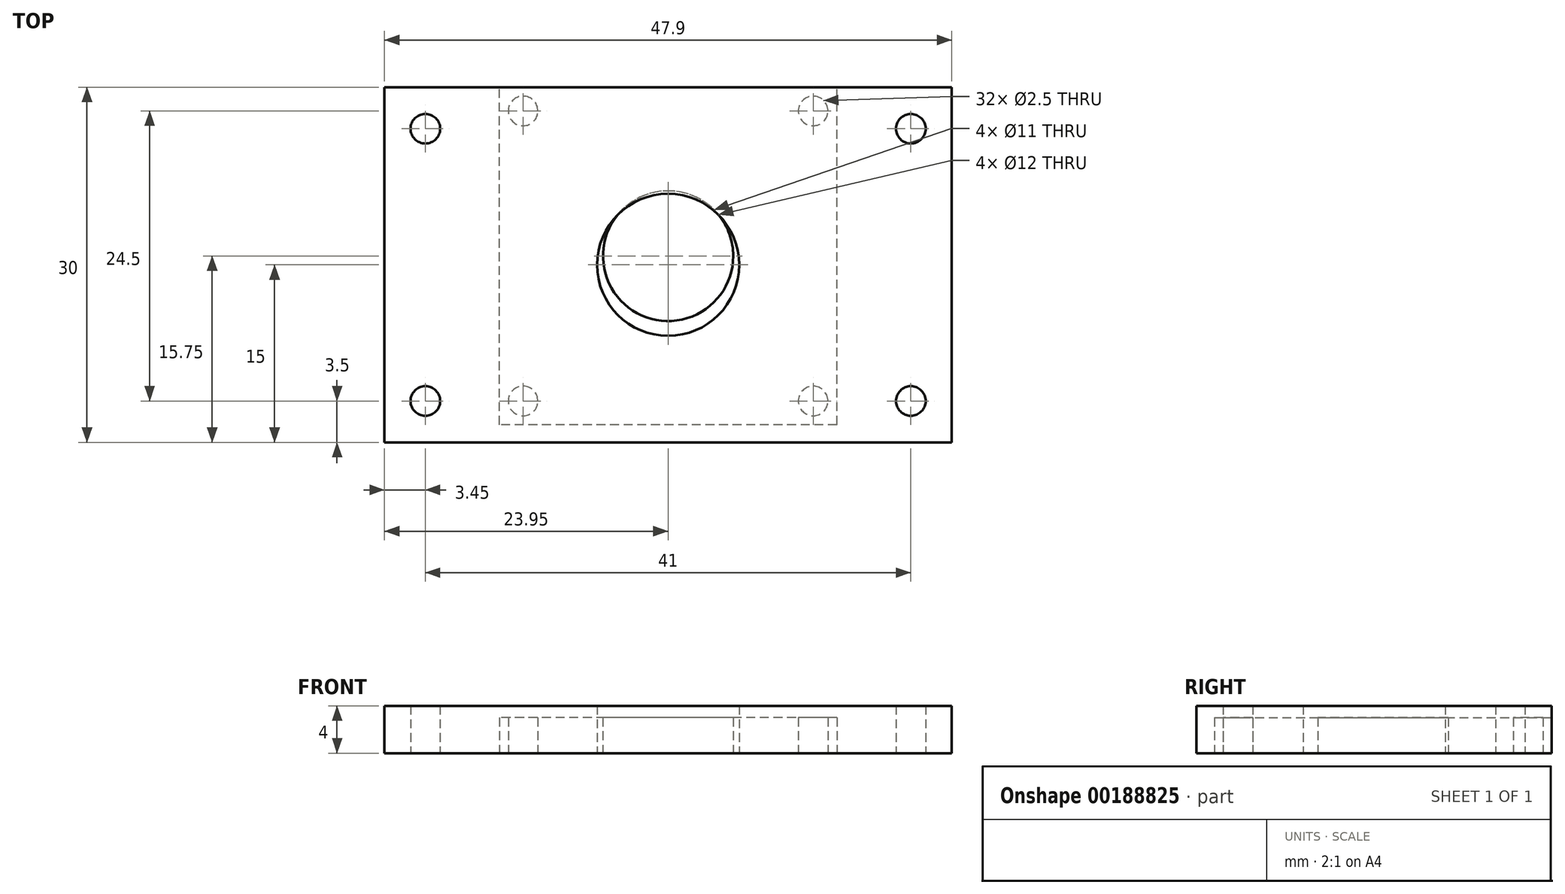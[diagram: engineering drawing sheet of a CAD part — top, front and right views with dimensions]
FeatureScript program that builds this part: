
annotation { "Feature Type Name" : "Feature", "Feature Type Description" : "" }
export const myFeature = defineFeature(function(context is Context, id is Id, definition is map)
    precondition{}
    {
        {
            var Q0;
            Q0=qCreatedBy(makeId("Top.planeOp"),FACE);
            var sketch = newSketch(context, id + "F0", { "sketchPlane" : qUnion([Q0])});
            skLineSegment(sketch, "E0.bottom", {"start": v(14.25, -14.25) * mm, "end": v(-14.25, -14.25) * mm});
            skLineSegment(sketch, "E0.top", {"start": v(14.25, 14.25) * mm, "end": v(-14.25, 14.25) * mm});
            skLineSegment(sketch, "E0.left", {"start": v(14.25, -14.25) * mm, "end": v(14.25, 14.25) * mm});
            skLineSegment(sketch, "E0.right", {"start": v(-14.25, -14.25) * mm, "end": v(-14.25, 14.25) * mm});
            skPoint(sketch, "E0.middle", {"position": v(0, 0) * mm});
            skLineSegment(sketch, "E1.bottom", {"start": v(12.25, 12.25) * mm, "end": v(-12.25, 12.25) * mm, "construction": true});
            skLineSegment(sketch, "E1.top", {"start": v(12.25, -12.25) * mm, "end": v(-12.25, -12.25) * mm, "construction": true});
            skLineSegment(sketch, "E1.left", {"start": v(12.25, 12.25) * mm, "end": v(12.25, -12.25) * mm, "construction": true});
            skLineSegment(sketch, "E1.right", {"start": v(-12.25, 12.25) * mm, "end": v(-12.25, -12.25) * mm, "construction": true});
            skCircle(sketch, "E2", {"center": v(-12.25, 12.25) * mm, "radius": 1.25 * mm});
            skCircle(sketch, "E3", {"center": v(12.25, 12.25) * mm, "radius": 1.25 * mm});
            skCircle(sketch, "E4", {"center": v(-12.25, -12.25) * mm, "radius": 1.25 * mm});
            skCircle(sketch, "E5", {"center": v(12.25, -12.25) * mm, "radius": 1.25 * mm});
            skCircle(sketch, "E6", {"center": v(0, 0) * mm, "radius": 5.5 * mm});
            skSolve(sketch);
        }
        {
            var Q0;
            Q0=makeQuery(id+"F0.imprint","IMPRINT",FACE,{"disambiguationData":[TD([[makeQuery(id+"F0.imprint","IMPRINT",EDGE,{"derivedFrom":sQuery(id+"F0.wireOp",EDGE,"E0.bottom")}),-1.0]])]});
            extrude(context, id + "F1", {"entities" : qUnion([Q0]), "depth" : 3 * mm});
        }
        {
            var Q0;
            Q0=qCreatedBy(makeId("Top.planeOp"),FACE);
            var sketch = newSketch(context, id + "F2", { "sketchPlane" : qUnion([Q0])});
            skLineSegment(sketch, "E7.bottom", {"start": v(23.95, -15.75) * mm, "end": v(-23.95, -15.75) * mm});
            skLineSegment(sketch, "E7.top", {"start": v(23.95, 14.25) * mm, "end": v(-23.95, 14.25) * mm});
            skLineSegment(sketch, "E7.left", {"start": v(23.95, -15.75) * mm, "end": v(23.95, 14.25) * mm});
            skLineSegment(sketch, "E7.right", {"start": v(-23.95, -15.75) * mm, "end": v(-23.95, 14.25) * mm});
            skPoint(sketch, "E7.middle", {"position": v(0, -0.75) * mm});
            skLineSegment(sketch, "E8.bottom", {"start": v(20.5, 10.75) * mm, "end": v(-20.5, 10.75) * mm, "construction": true});
            skLineSegment(sketch, "E8.top", {"start": v(20.5, -12.25) * mm, "end": v(-20.5, -12.25) * mm, "construction": true});
            skLineSegment(sketch, "E8.left", {"start": v(20.5, 10.75) * mm, "end": v(20.5, -12.25) * mm, "construction": true});
            skLineSegment(sketch, "E8.right", {"start": v(-20.5, 10.75) * mm, "end": v(-20.5, -12.25) * mm, "construction": true});
            skCircle(sketch, "E9", {"center": v(-20.5, 10.75) * mm, "radius": 1.25 * mm});
            skCircle(sketch, "E10", {"center": v(20.5, 10.75) * mm, "radius": 1.25 * mm});
            skCircle(sketch, "E11", {"center": v(-20.5, -12.25) * mm, "radius": 1.25 * mm});
            skCircle(sketch, "E12", {"center": v(20.5, -12.25) * mm, "radius": 1.25 * mm});
            skCircle(sketch, "E13", {"center": v(0, -0.75) * mm, "radius": 6 * mm});
            skSolve(sketch);
        }
        {
            var Q0;
            Q0 = qSketchRegion(id + "F2", true);
            extrude(context, id + "F3", {"entities" : qUnion([Q0]), "depth" : 4 * mm, "offsetDistance" : 25 * mm});
        }
    });
